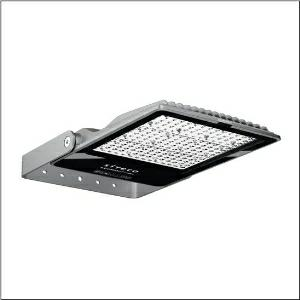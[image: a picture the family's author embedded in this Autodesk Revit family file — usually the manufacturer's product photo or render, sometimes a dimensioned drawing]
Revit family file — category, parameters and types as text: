
# Revit family: sicompact_r__31_midi___pl32_5xa7581e2k23_2195
name_source: partatom
category: Lighting Fixtures
units: mm (PartAtom-declared; Revit-internal decimal feet)

## family parameters
Cut with Voids When Loaded = No
Host = Face
Light Source = No
Part Type = Normal
Room Calculation Point = No
Round Connector Dimension = Use Diameter
Shared = No

## types (1)
- SiCompact® 31 midi  PL32 (1 x LED, 37000 lm, 243 W, 4000K)
    Apparent Load = 243 VA
    CIE Flux Codes = 32 69 98 100 100
    Color Rendering = 70
    Color Temperature = 4000K
    Default Elevation = 1800 mm
    Description = SiCompact® 31 midi, floodlight, primary light control with lens, of plastic, of toughened safety glass, transparent, light distribution: PL32, light emission: direct distribution, primary light characteristic: asymmetric, installation type: surface-mounted, LED, High Power LED, rated luminous flux: 37.000lm, luminous efficacy: 152lm/W, light colour: 740, colour temperature: 4000K, control gear: ON/OFF, with cable, 3x 1.5mm², mains connection: 220..240V, AC, 50/60Hz, connection cable pre-assembled, cable length: 2m, rated input power: 243W, of diecast aluminium, specular, metallic grey (RAL 9006), length: 560mm, width: 330mm, height: 62mm, bracket, of sheet steel, coated, metallic grey (RAL 9006), ON/OFF, protection rating (complete): IP66, insulation class (complete): insulation class I (protective earthing), certification: CE, ENEC, impact resistance: IK08, permissible operating ambient temperature: -40..+45°C, packaging unit: 1 piece

Light Distribution: PL32
    Height = 62 mm  [stored 0.203412 ft]
    Lamp = 1 x LED
    Lamp Light Flux = 37000 lm
    Lamp Power = 243 W
    Lamp count = 1
    Length = 560 mm
    Luminous efficacy = 152 lm/W
    Manufacturer = Siteco
    ModVariant = No
    Model = 5XA7581E2K23
    Mounting Place = Wall
    Mounting Type = Surface mounted
    Number of Poles = 1
    OnlyDefault = Yes
    Power Factor = 1
    Product Name = SiCompact® 31 midi | PL32
    Product group = floodlight | wall mounted
    ProductGroupID = 2001
    Protection Class = Protection class I
    Protection Degree = IP 66
    RLX_Detail_Level = 1
    RLX_Emergency_Light_Flux = 0 lm
    RLX_Emergency_Type = 0
    RLX_Emergency_Type_DB = No
    RlxData = <blob elided: 98205 chars, md5=f8208764>
    Socket = socket
    Standby Power = 0 W
    System Light Flux = 37000 lm
    System Power = 243 W
    Type Comments = Product without accessories
    Type Image = l_1006415.jpg
    URL = http://relux.com
    VarID = ---
    Voltage = 0 V
    Weight = 0.00 kg
    Width = 333 mm

note: [stored X ft] marks values corroborated as IEEE doubles in the binary element streams (Revit-internal decimal feet)

## geometry (parser evidence)
native form markers: Blend x4, Sweep x11
no freeform markers — native parametric forms only
